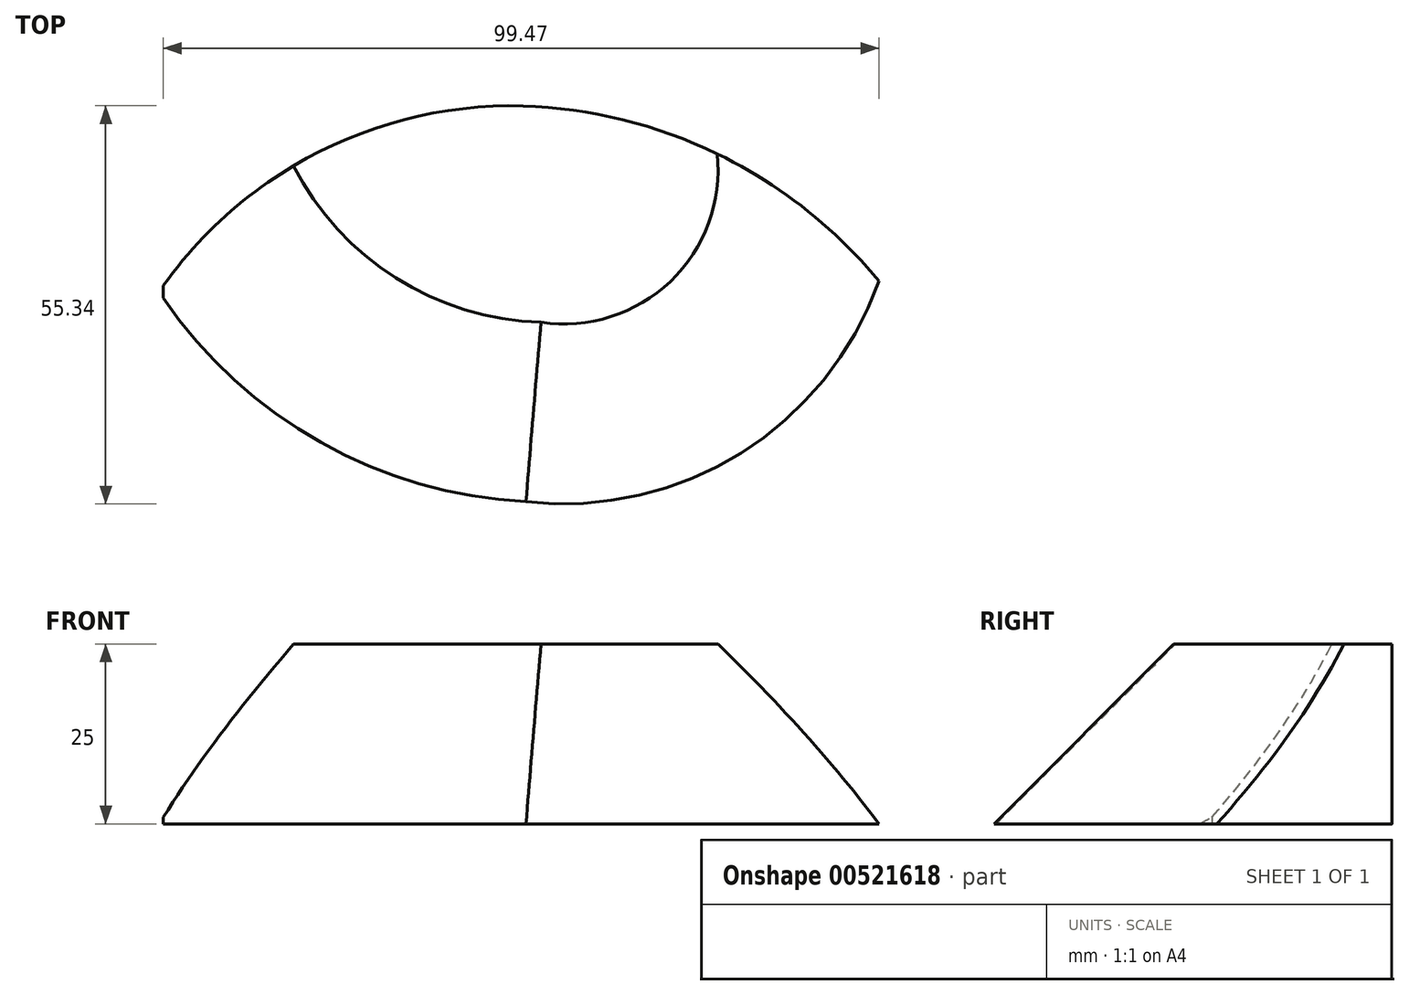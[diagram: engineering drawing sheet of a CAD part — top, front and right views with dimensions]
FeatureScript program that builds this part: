
annotation { "Feature Type Name" : "Feature", "Feature Type Description" : "" }
export const myFeature = defineFeature(function(context is Context, id is Id, definition is map)
    precondition{}
    {
        {
            var Q0;
            Q0=qCreatedBy(makeId("Top.planeOp"),FACE);
            var sketch = newSketch(context, id + "F0", { "sketchPlane" : qUnion([Q0])});
            skLineSegment(sketch, "E0", {"start": v(0, 0) * mm, "end": v(-50, 0) * mm});
            skLineSegment(sketch, "E1", {"start": v(0, 0) * mm, "end": v(50, 0) * mm});
            skLineSegment(sketch, "E2", {"start": v(0, 0) * mm, "end": v(0, 30) * mm});
            skLineSegment(sketch, "E3", {"start": v(0, 0) * mm, "end": v(0, -30) * mm});
            skLineSegment(sketch, "E4", {"start": v(-14.04, 0) * mm, "end": v(-14.04, 5) * mm});
            skLineSegment(sketch, "E5", {"start": v(-14.04, 0) * mm, "end": v(-14.04, -5) * mm});
            skLineSegment(sketch, "E6", {"start": v(-50, 5) * mm, "end": v(-50, -5) * mm});
            skLineSegment(sketch, "E7", {"start": v(-50, -5) * mm, "end": v(50, -5) * mm});
            skLineSegment(sketch, "E8", {"start": v(50, -5) * mm, "end": v(50, 5) * mm});
            skLineSegment(sketch, "E9", {"start": v(50, 5) * mm, "end": v(-50, 5) * mm});
            skArc(sketch, "E10", {"start": v(50, 5) * mm, "mid": v(27.74, 22.97) * mm, "end": v(0, 30) * mm});
            skArc(sketch, "E11", {"start": v(0, 30) * mm, "mid": v(-28.12, 23.74) * mm, "end": v(-50, 5) * mm});
            skArc(sketch, "E12", {"start": v(-50, -5) * mm, "mid": v(-27.6, -22.71) * mm, "end": v(0, -30) * mm});
            skArc(sketch, "E13", {"start": v(0, -30) * mm, "mid": v(28.7, -24.9) * mm, "end": v(50, -5) * mm});
            skSolve(sketch);
        }
        {
            var Q0;
            {var subQ0=sQuery(id+"F0.wireOp",EDGE,"E10");Q0=makeQuery(id+"F0.imprint","IMPRINT",FACE,{"disambiguationData":[TD([[makeQuery(id+"F0.imprint","IMPRINT",EDGE,{"derivedFrom":subQ0}),1.0]])]});}
            var Q1;
            {var subQ0=sQuery(id+"F0.wireOp",EDGE,"E13");Q1=makeQuery(id+"F0.imprint","IMPRINT",FACE,{"disambiguationData":[TD([[makeQuery(id+"F0.imprint","IMPRINT",EDGE,{"derivedFrom":subQ0}),1.0]])]});}
            var Q2;
            {var subQ3=sQuery(id+"F0.wireOp",EDGE,"E4");Q2=makeQuery(id+"F0.imprint","IMPRINT",FACE,{"disambiguationData":[TD([[makeQuery(id+"F0.imprint","IMPRINT",EDGE,{"derivedFrom":subQ3}),1.0]])]});}
            var Q3;
            {var subQ3=sQuery(id+"F0.wireOp",EDGE,"E5");Q3=makeQuery(id+"F0.imprint","IMPRINT",FACE,{"disambiguationData":[TD([[makeQuery(id+"F0.imprint","IMPRINT",EDGE,{"derivedFrom":subQ3}),-1.0]])]});}
            var Q4;
            {var subQ0=sQuery(id+"F0.wireOp",EDGE,"E1");Q4=makeQuery(id+"F0.imprint","IMPRINT",FACE,{"disambiguationData":[TD([[makeQuery(id+"F0.imprint","IMPRINT",EDGE,{"derivedFrom":subQ0}),1.0]])]});}
            var Q5;
            {var subQ0=sQuery(id+"F0.wireOp",EDGE,"E1");Q5=makeQuery(id+"F0.imprint","IMPRINT",FACE,{"disambiguationData":[TD([[makeQuery(id+"F0.imprint","IMPRINT",EDGE,{"derivedFrom":subQ0}),-1.0]])]});}
            var Q6;
            {var subQ0=sQuery(id+"F0.wireOp",EDGE,"E12");Q6=makeQuery(id+"F0.imprint","IMPRINT",FACE,{"disambiguationData":[TD([[makeQuery(id+"F0.imprint","IMPRINT",EDGE,{"derivedFrom":subQ0}),1.0]])]});}
            var Q7;
            {var subQ0=sQuery(id+"F0.wireOp",EDGE,"E11");Q7=makeQuery(id+"F0.imprint","IMPRINT",FACE,{"disambiguationData":[TD([[makeQuery(id+"F0.imprint","IMPRINT",EDGE,{"derivedFrom":subQ0}),1.0]])]});}
            var Q8;
            {var subQ3=sQuery(id+"F0.wireOp",EDGE,"E5");Q8=makeQuery(id+"F0.imprint","IMPRINT",FACE,{"disambiguationData":[TD([[makeQuery(id+"F0.imprint","IMPRINT",EDGE,{"derivedFrom":subQ3}),1.0]])]});}
            var Q9;
            {var subQ3=sQuery(id+"F0.wireOp",EDGE,"E4");Q9=makeQuery(id+"F0.imprint","IMPRINT",FACE,{"disambiguationData":[TD([[makeQuery(id+"F0.imprint","IMPRINT",EDGE,{"derivedFrom":subQ3}),-1.0]])]});}
            extrude(context, id + "F1", {"entities" : qUnion([Q0, Q1, Q2, Q3, Q4, Q5, Q6, Q7, Q8, Q9]), "depth" : 25 * mm, "offsetDistance" : 25 * mm});
        }
        {
            var Q0;
            Q0=makeQuery(id+"F1.opExtrude","CAP_EDGE",EDGE,{"disambiguationData":[OSD([sQuery(id+"F0.wireOp",EDGE,"E12")])],"isStart":false});
            var Q1;
            Q1=makeQuery(id+"F1.opExtrude","CAP_EDGE",EDGE,{"disambiguationData":[OSD([sQuery(id+"F0.wireOp",EDGE,"E13")])],"isStart":false});
            chamfer(context, id + "F2", {"entities" : qUnion([Q0, Q1]), "width" : 30 * mm, "tangentPropagation" : true});
        }
    });
